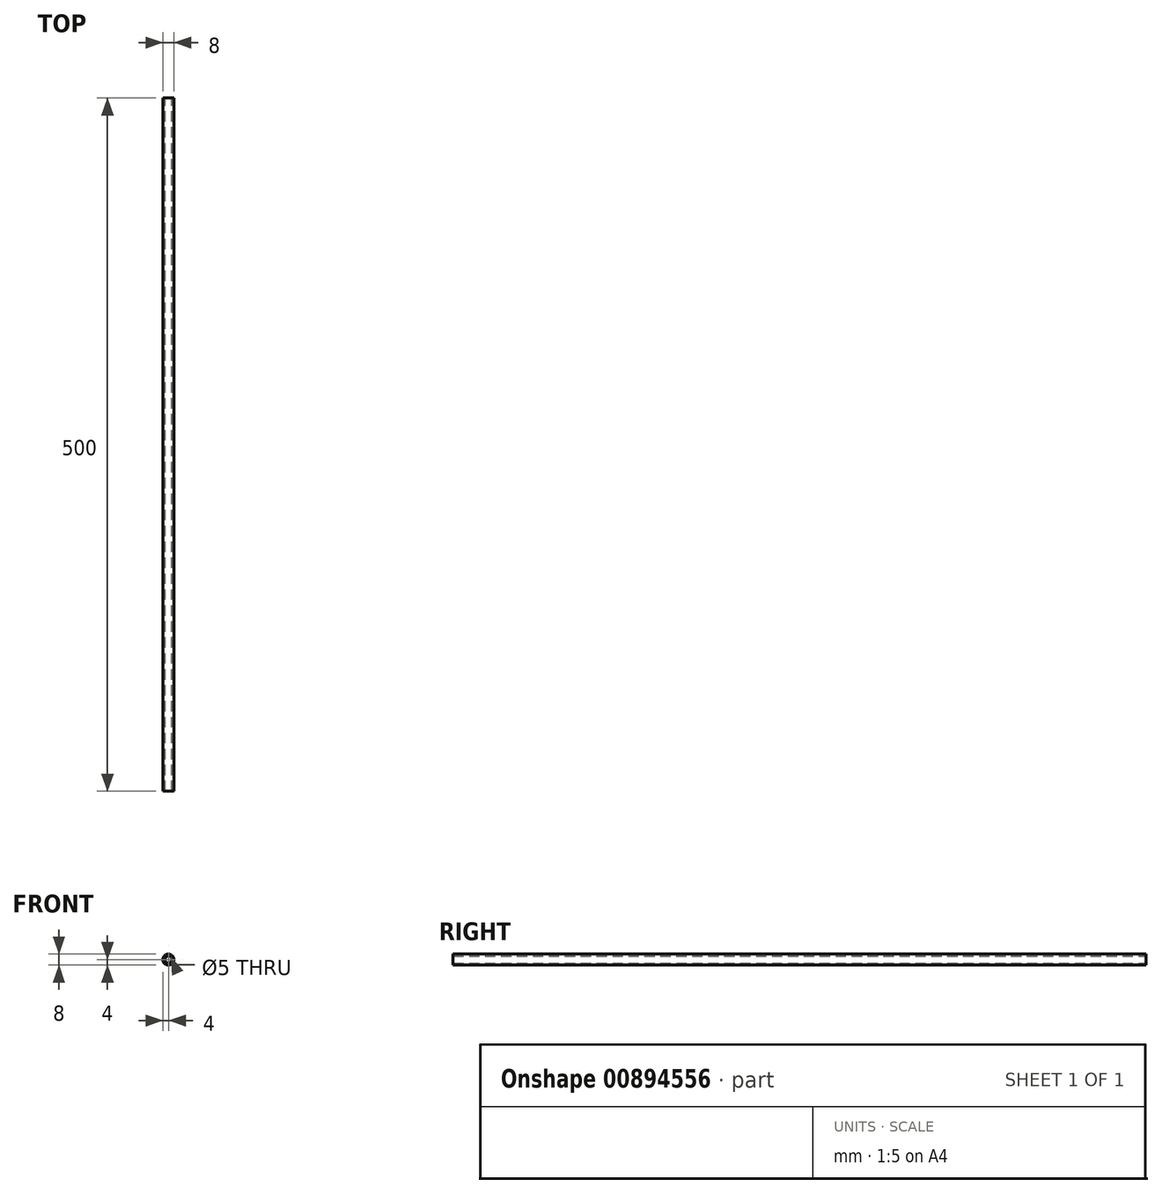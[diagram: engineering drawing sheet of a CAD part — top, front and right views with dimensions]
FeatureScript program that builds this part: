
annotation { "Feature Type Name" : "Feature", "Feature Type Description" : "" }
export const myFeature = defineFeature(function(context is Context, id is Id, definition is map)
    precondition{}
    {
        {
            var Q0;
            Q0=qCreatedBy(makeId("Front.planeOp"),FACE);
            var sketch = newSketch(context, id + "F0", { "sketchPlane" : qUnion([Q0])});
            skCircle(sketch, "E0", {"center": v(0, 0) * mm, "radius": 4 * mm});
            skCircle(sketch, "E1", {"center": v(0, 0) * mm, "radius": 2.5 * mm});
            skSolve(sketch);
        }
        {
            var Q0;
            Q0 = qSketchRegion(id + "F0", true);
            extrude(context, id + "F1", {"entities" : qUnion([Q0]), "depth" : 500 * mm, "offsetDistance" : 25 * mm});
        }
    });
